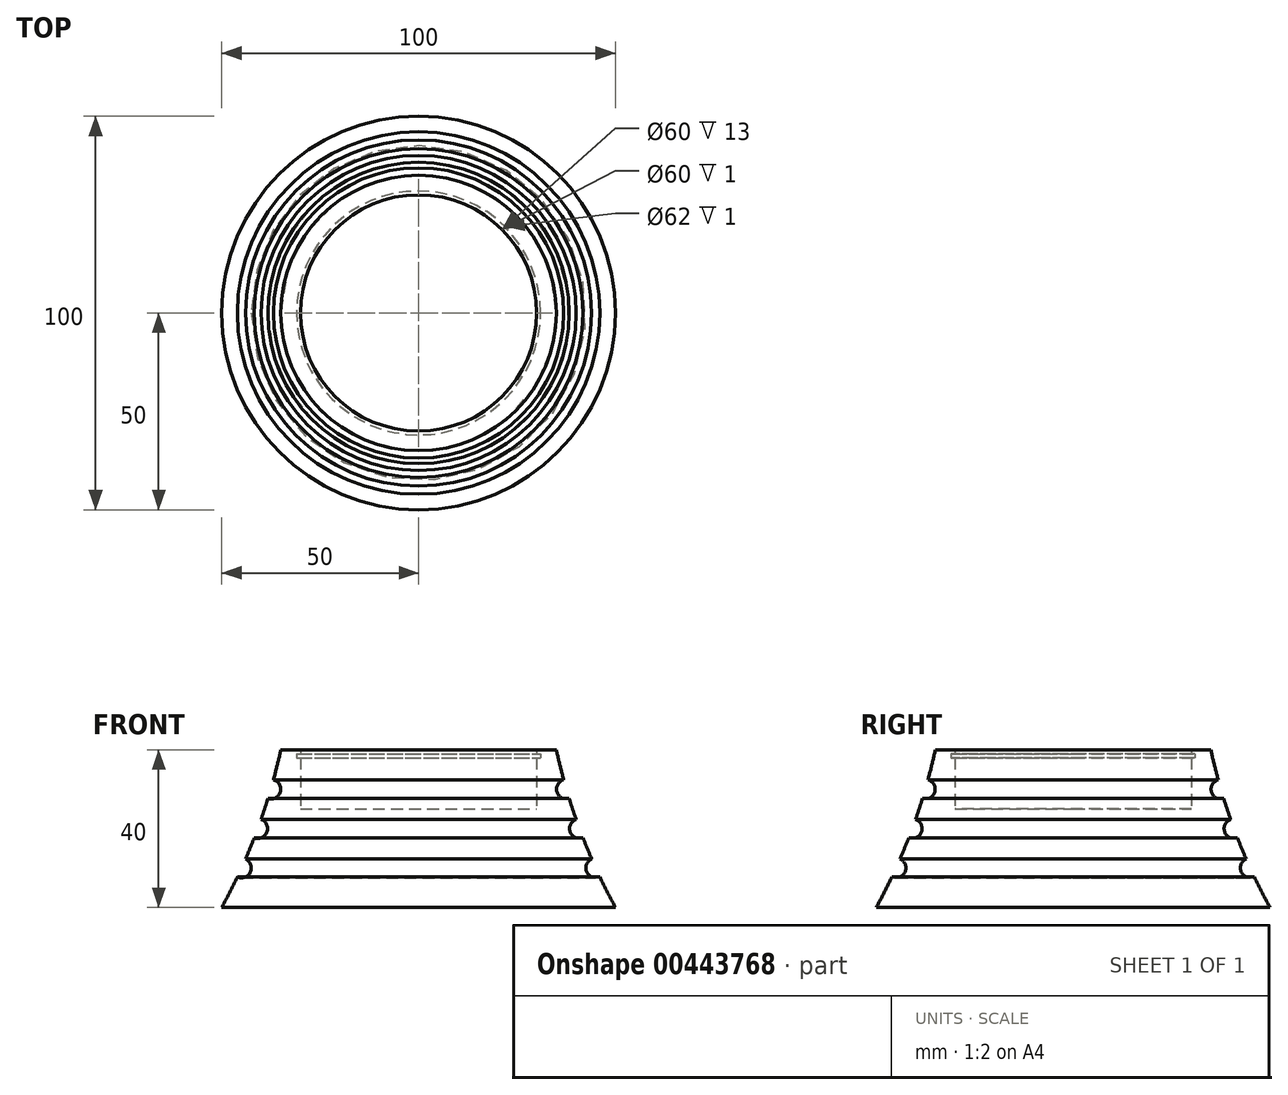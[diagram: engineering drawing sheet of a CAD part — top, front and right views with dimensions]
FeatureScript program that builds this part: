
annotation { "Feature Type Name" : "Feature", "Feature Type Description" : "" }
export const myFeature = defineFeature(function(context is Context, id is Id, definition is map)
    precondition{}
    {
        {
            var Q0;
            Q0=qCreatedBy(makeId("Front.planeOp"),FACE);
            var sketch = newSketch(context, id + "F0", { "sketchPlane" : qUnion([Q0])});
            skLineSegment(sketch, "E0", {"start": v(0, 0) * mm, "end": v(0, 25) * mm});
            skLineSegment(sketch, "E1", {"start": v(0, 25) * mm, "end": v(30, 25) * mm});
            skLineSegment(sketch, "E2", {"start": v(30, 25) * mm, "end": v(30, 38) * mm});
            skLineSegment(sketch, "E3", {"start": v(30, 40) * mm, "end": v(35, 40) * mm});
            skLineSegment(sketch, "E4", {"start": v(0, 0) * mm, "end": v(50, 0) * mm});
            skArc(sketch, "E5", {"start": v(35, 40) * mm, "mid": v(35.89, 36.2) * mm, "end": v(36.87, 32.4) * mm});
            skLineSegment(sketch, "E6.bottom", {"start": v(30, 39) * mm, "end": v(31, 39) * mm});
            skLineSegment(sketch, "E6.top", {"start": v(30, 38) * mm, "end": v(31, 38) * mm});
            skLineSegment(sketch, "E6.right", {"start": v(31, 39) * mm, "end": v(31, 38) * mm});
            skLineSegment(sketch, "E7.trimOffspring", {"start": v(30, 39) * mm, "end": v(30, 40) * mm});
            skArc(sketch, "E8", {"start": v(36.87, 32.4) * mm, "mid": v(35.16, 29.3) * mm, "end": v(38.28, 27.6) * mm});
            skArc(sketch, "E9", {"start": v(40.02, 22.35) * mm, "mid": v(38.52, 19.13) * mm, "end": v(41.76, 17.66) * mm});
            skArc(sketch, "E10", {"start": v(43.97, 12.28) * mm, "mid": v(42.72, 8.96) * mm, "end": v(46.05, 7.73) * mm});
            skArc(sketch, "E11.trimOffspring", {"start": v(38.28, 27.6) * mm, "mid": v(39.12, 24.97) * mm, "end": v(40.02, 22.35) * mm});
            skArc(sketch, "E12.trimOffspring", {"start": v(46.05, 7.73) * mm, "mid": v(47.97, 3.84) * mm, "end": v(50, 0) * mm});
            skArc(sketch, "E13.trimOffspring", {"start": v(41.76, 17.66) * mm, "mid": v(42.84, 14.96) * mm, "end": v(43.97, 12.28) * mm});
            skSolve(sketch);
        }
        {
            var Q0;
            Q0 = qSketchRegion(id + "F0", true);
            var Q1;
            Q1=sQuery(id+"F0.wireOp",EDGE,"E0");
            revolve(context, id + "F1", {"entities" : qUnion([Q0]), "axis" : qUnion([Q1]), "revolveType" : RevolveType.FULL});
        }
    });
